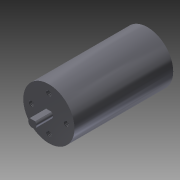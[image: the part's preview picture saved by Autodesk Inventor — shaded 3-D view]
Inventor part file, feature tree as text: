
AUTODESK INVENTOR PART (.ipt)
format: ipt  version: 2014 (Build 180170000, 170)  size: 114,176 bytes
history: native  units: mm
features: sketch x3, extrude x2, other x1, hole x1
ambient origin geometry x8: Origin, YZ Plane, XZ Plane, XY Plane, X Axis, Y Axis, Z Axis, Center Point
bodies: Body1 (feature_tree)
feature tree (7):
  other  "Sólido1"
  extrude  "Extrusión1"  Depth=48.006mm TaperAngle=0.0deg
  extrude  "Extrusión2"  Depth=1.5mm
  hole  "Hole1"  [1 undecoded]
  sketch  "Boceto1"  dims[d0=24.892mm d1=48.006mm d2=0.0mm]
  sketch  "Boceto2"  dims[d3=4.0mm d4=1.5mm]
  sketch  "Boceto3"  dims[d5=8.001mm d6=0.0mm d7=8.5mm d8=40.0mm d10=360.0deg d12=2.459mm d13=5.0mm d14=4.0mm d15=2.0mm d16=90.0deg d17=6.0mm d18=20.594885mm]
note: 1 required parameter value undecoded (feature->parameter linkage not recoverable at this tier; creation-order binding heuristic only, values carry confidence <= 0.55)
